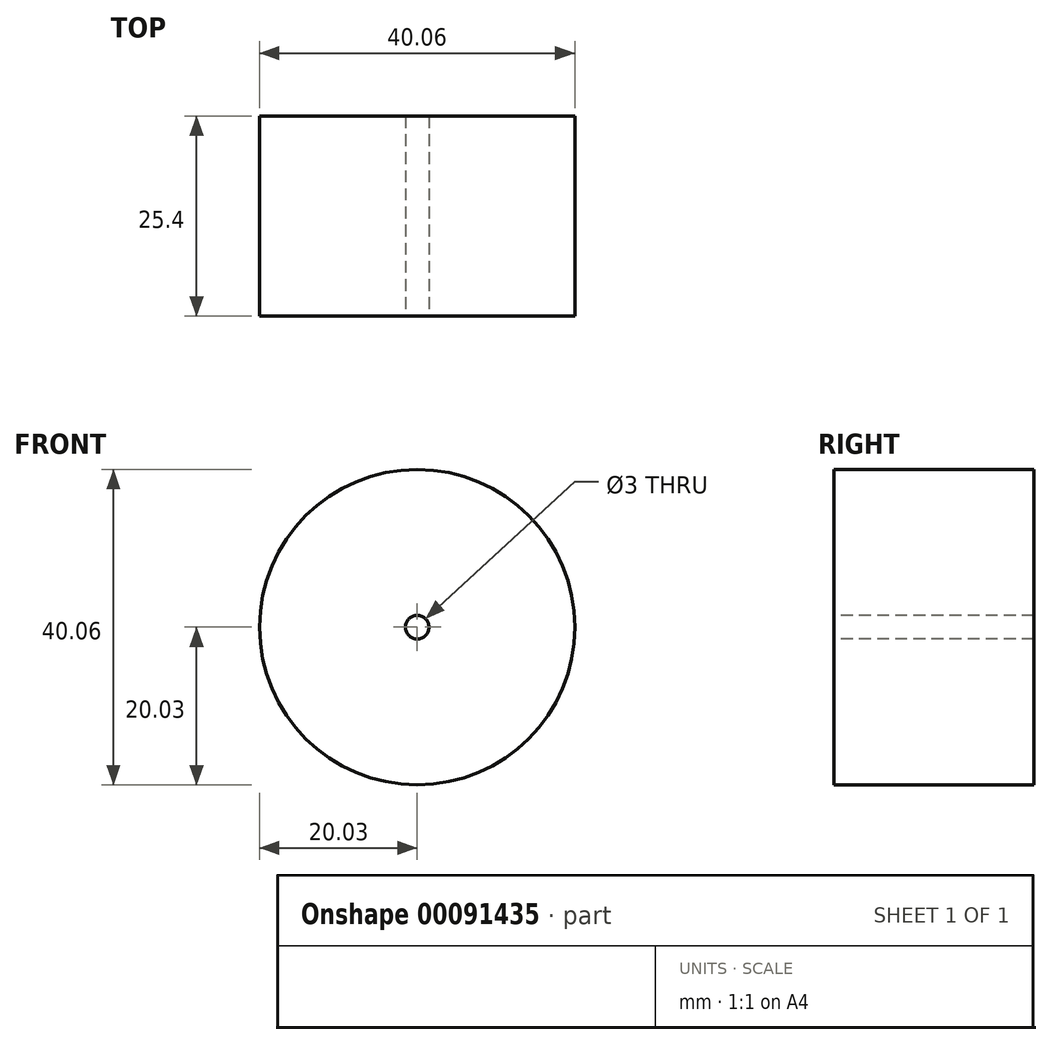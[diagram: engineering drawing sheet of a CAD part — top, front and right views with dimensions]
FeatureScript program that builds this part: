
annotation { "Feature Type Name" : "Feature", "Feature Type Description" : "" }
export const myFeature = defineFeature(function(context is Context, id is Id, definition is map)
    precondition{}
    {
        {
            var Q0;
            Q0=qCreatedBy(makeId("Front.planeOp"),FACE);
            var sketch = newSketch(context, id + "F0", { "sketchPlane" : qUnion([Q0])});
            skCircle(sketch, "E0", {"center": v(0, 0) * mm, "radius": 20.03 * mm});
            skSolve(sketch);
        }
        {
            var Q0;
            Q0=makeQuery(id+"F0.imprint","IMPRINT",FACE,{"disambiguationData":[TD([[makeQuery(id+"F0.imprint","IMPRINT",EDGE,{"derivedFrom":sQuery(id+"F0.wireOp",EDGE,"E0")}),1.0]])]});
            var sketch = newSketch(context, id + "F1", { "sketchPlane" : qUnion([Q0])});
            skCircle(sketch, "E1", {"center": v(0, 0) * mm, "radius": 1.5 * mm});
            skSolve(sketch);
        }
        {
            var Q0;
            Q0=makeQuery(id+"F0.imprint","IMPRINT",FACE,{"disambiguationData":[TD([[makeQuery(id+"F0.imprint","IMPRINT",EDGE,{"derivedFrom":sQuery(id+"F0.wireOp",EDGE,"E0")}),1.0]])]});
            extrude(context, id + "F2", {"entities" : qUnion([Q0]), "depth" : 25.4 * mm});
        }
        {
            var Q0;
            Q0=makeQuery(id+"F2.opExtrude","CAP_FACE",FACE,{"disambiguationData":[OSD([sQuery(id+"F0.wireOp",EDGE,"E0")])],"isStart":false});
            var sketch = newSketch(context, id + "F3", { "sketchPlane" : qUnion([Q0])});
            skCircle(sketch, "E2", {"center": v(0, 0) * mm, "radius": 1.41 * mm});
            skSolve(sketch);
        }
        {
            var Q0;
            Q0 = qSketchRegion(id + "F1", true);
            extrude(context, id + "F4", {"entities" : qUnion([Q0]), "operationType" : NewBodyOperationType.ADD, "oppositeDirection" : true, "depth" : 25.4 * mm});
        }
        {
            var Q0;
            Q0=sQuery(id+"F3.wireOp",VERTEX,"E2.center");
            var Q1;
            Q1=makeQuery(id+"F2.opExtrude","SWEPT_BODY",BODY,{"disambiguationData":[OSD([sQuery(id+"F0.wireOp",EDGE,"E0")])]});
            hole(context, id + "F5", {"style" : HoleStyle.SIMPLE, "endStyle" : HoleEndStyle.THROUGH, "holeDiameter" : 3 * mm, "locations" : qUnion([Q0]), "scope" : qUnion([Q1]), "isTappedThrough" : true});
        }
    });
